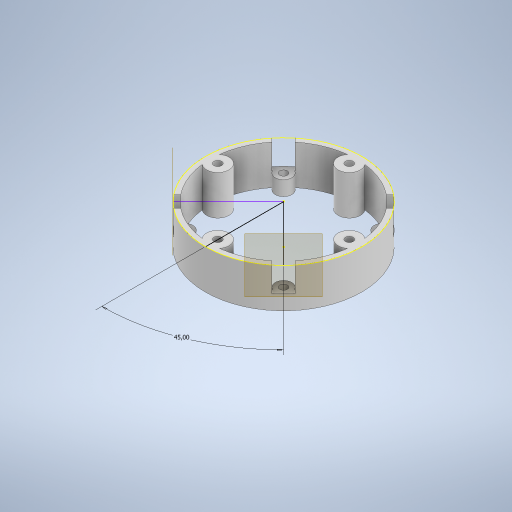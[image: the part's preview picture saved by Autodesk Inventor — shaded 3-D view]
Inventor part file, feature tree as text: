
AUTODESK INVENTOR PART (.ipt)
format: ipt  version: 2024 (Build 280153000, 153)  size: 397,312 bytes
history: native  units: in
note: dims shown in document units (in); Inventor stores cm internally (conversion verified against a paired STEP export)
features: sketch x9, extrude x6, plane x2
ambient origin geometry x8: Origin, YZ Plane, XZ Plane, XY Plane, X Axis, Y Axis, Z Axis, Center Point
bodies: Solid1 (feature_tree)
feature tree (17):
  extrude  "Walls"  Depth=2.3228in
  extrude  "Pillar holes"  Depth=0.626in
  sketch  "Sketch4"  dims[d5=0.2165in d6=0.3543in]
  sketch  "Sketch5"  dims[d7=1.5748in d9=360.0deg d11=0.626in d12=0.0in]
  extrude  "Extrusion4"  Depth=0.3543in
  sketch  "Sketch7"  dims[d25=0.315in d26=0.0in d27=45.0deg]
  plane  "Work Plane1"
  plane  "Work Plane2"
  extrude  "Extrusion13"  Depth=0.626in TaperAngle=0.0deg
  extrude  "Extrusion14"  Depth=1.5748in TaperAngle=360.0deg
  extrude  "Extrusion15"  TaperAngle=45.0deg  [1 undecoded]
  sketch  "Sketch1"  dims[d0=2.4803in d1=2.3228in]
  sketch  "Sketch2"  dims[d2=0.626in d3=0.0in d4=0.1969in]
  sketch  "Sketch6"  dims[d20=0.122in d21=1.5748in d23=360.0deg]
  sketch  "Sketch17"  dims[d86=1.2402in]
  sketch  "Sketch18"  dims[d87=45.0deg]
  sketch  "Sketch19"  dims[d88=0.1314in d89=0.122in d90=1.5748in d92=360.0deg d94=0.626in d95=0.0in d96=45.0deg d97=0.1314in d98=0.122in d99=1.5748in d101=360.0deg d103=0.626in d104=0.0in d105=1.5748in d107=360.0deg d109=0.3937in d110=0.0in]
note: 1 required parameter value undecoded (feature->parameter linkage not recoverable at this tier; creation-order binding heuristic only, values carry confidence <= 0.55)
